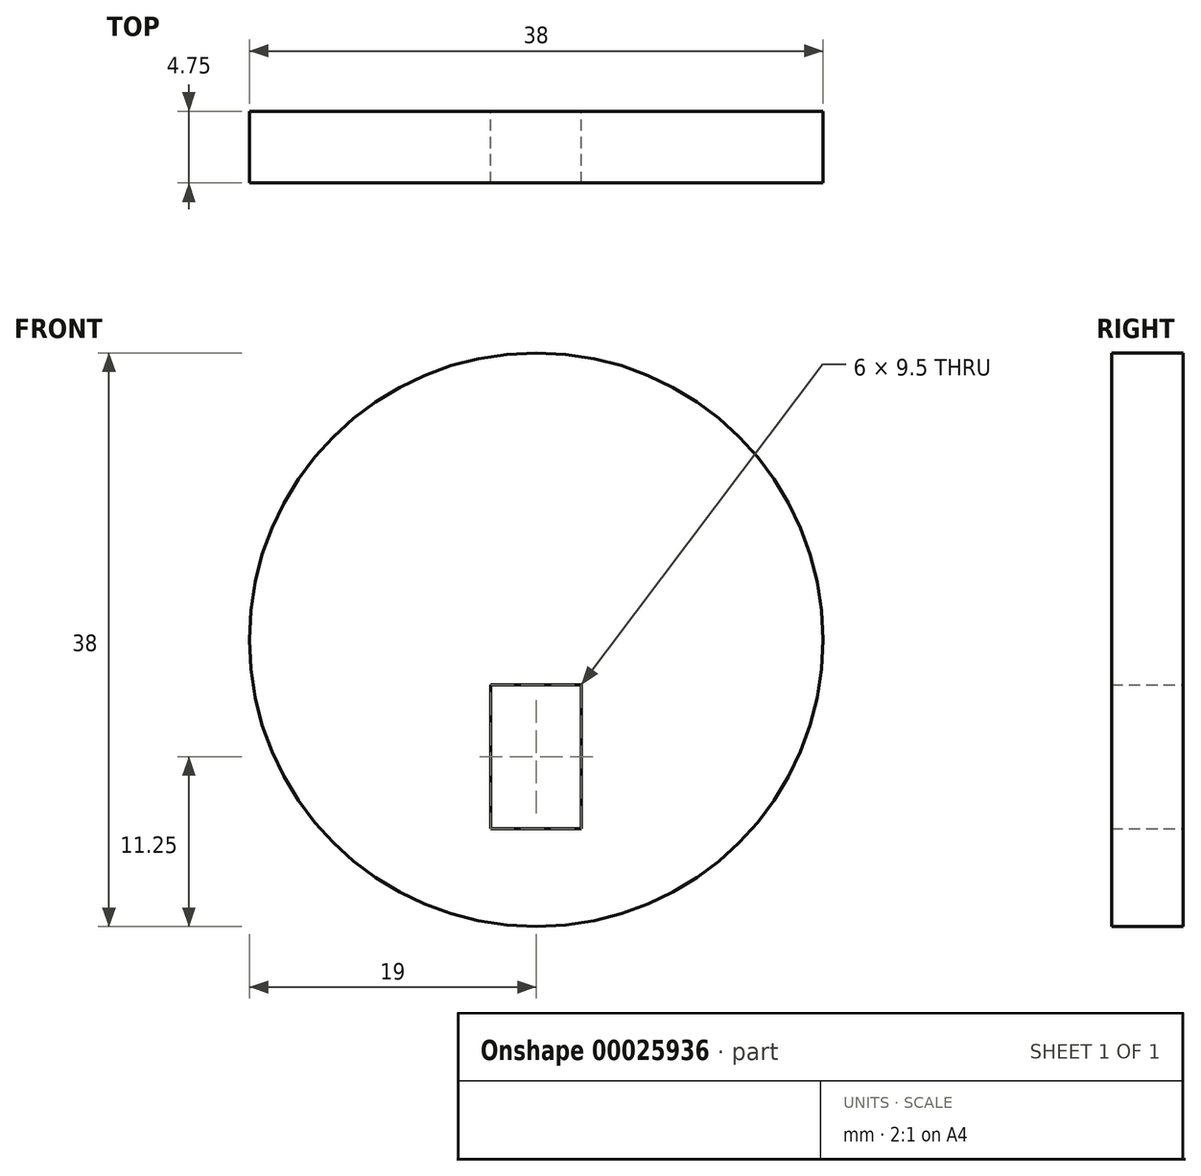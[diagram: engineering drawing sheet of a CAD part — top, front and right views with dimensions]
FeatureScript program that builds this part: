
annotation { "Feature Type Name" : "Feature", "Feature Type Description" : "" }
export const myFeature = defineFeature(function(context is Context, id is Id, definition is map)
    precondition{}
    {
        {
            var Q0;
            Q0=qCreatedBy(makeId("Front.planeOp"),FACE);
            var sketch = newSketch(context, id + "F0", { "sketchPlane" : qUnion([Q0])});
            skCircle(sketch, "E0", {"center": v(0, 0) * mm, "radius": 19 * mm});
            skLineSegment(sketch, "E1", {"start": v(0, -3) * mm, "end": v(-3, -3) * mm});
            skLineSegment(sketch, "E2", {"start": v(-3, -3) * mm, "end": v(-3, -12.5) * mm});
            skLineSegment(sketch, "E3", {"start": v(-3, -12.5) * mm, "end": v(0, -12.5) * mm});
            skLineSegment(sketch, "E4.MirrorCS", {"start": v(0, -3) * mm, "end": v(3, -3) * mm});
            skLineSegment(sketch, "E5.MirrorCS", {"start": v(3, -3) * mm, "end": v(3, -12.5) * mm});
            skLineSegment(sketch, "E6.MirrorCS", {"start": v(3, -12.5) * mm, "end": v(0, -12.5) * mm});
            skSolve(sketch);
        }
        {
            var Q0;
            Q0=makeQuery(id+"F0.imprint","IMPRINT",FACE,{"disambiguationData":[TD([[makeQuery(id+"F0.imprint","IMPRINT",EDGE,{"derivedFrom":sQuery(id+"F0.wireOp",EDGE,"E0")}),1.0]])]});
            extrude(context, id + "F1", {"entities" : qUnion([Q0]), "depth" : 4.75 * mm});
        }
    });
